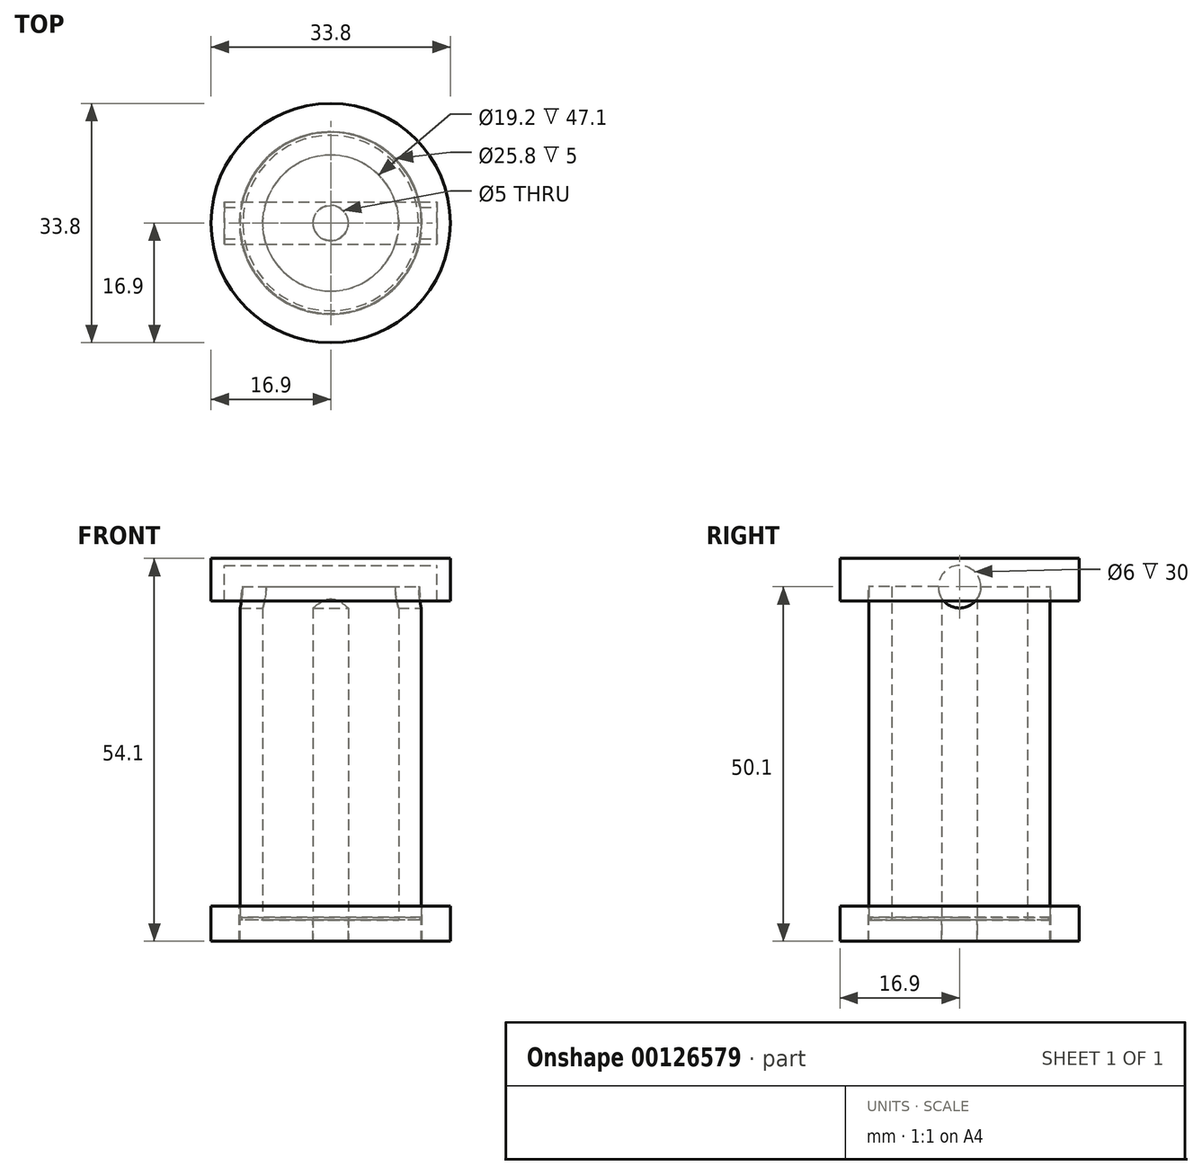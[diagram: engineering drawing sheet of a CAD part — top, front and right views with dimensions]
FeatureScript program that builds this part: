
annotation { "Feature Type Name" : "Feature", "Feature Type Description" : "" }
export const myFeature = defineFeature(function(context is Context, id is Id, definition is map)
    precondition{}
    {
        {
            var Q0;
            Q0=qCreatedBy(makeId("Top.planeOp"),FACE);
            var sketch = newSketch(context, id + "F0", { "sketchPlane" : qUnion([Q0])});
            skCircle(sketch, "E0", {"center": v(0, 0) * mm, "radius": 9.6 * mm});
            skCircle(sketch, "E1", {"center": v(0, 0) * mm, "radius": 12.8 * mm});
            skCircle(sketch, "E2", {"center": v(0, 0) * mm, "radius": 2.5 * mm});
            skSolve(sketch);
        }
        {
            var Q0;
            Q0=makeQuery(id+"F0.imprint","IMPRINT",FACE,{"disambiguationData":[TD([[makeQuery(id+"F0.imprint","IMPRINT",EDGE,{"derivedFrom":sQuery(id+"F0.wireOp",EDGE,"E0")}),-1.0]])]});
            var Q1;
            Q1=makeQuery(id+"F0.imprint","IMPRINT",FACE,{"disambiguationData":[TD([[makeQuery(id+"F0.imprint","IMPRINT",EDGE,{"derivedFrom":sQuery(id+"F0.wireOp",EDGE,"E2")}),1.0]])]});
            extrude(context, id + "F1", {"entities" : qUnion([Q0, Q1]), "depth" : 47.1 * mm, "symmetric" : true});
        }
        {
            var Q0;
            Q0=makeQuery(id+"F1.opExtrude","CAP_FACE",FACE,{"disambiguationData":[OSD([sQuery(id+"F0.wireOp",EDGE,"E2")])],"isStart":false});
            var sketch = newSketch(context, id + "F2", { "sketchPlane" : qUnion([Q0])});
            skCircle(sketch, "E3", {"center": v(0, 0) * mm, "radius": 16.9 * mm});
            skCircle(sketch, "E4", {"center": v(0, 0) * mm, "radius": 12.9 * mm});
            skSolve(sketch);
        }
        {
            var Q0;
            Q0=makeQuery(id+"F2.imprint","IMPRINT",FACE,{"disambiguationData":[TD([[makeQuery(id+"F2.imprint","IMPRINT",EDGE,{"derivedFrom":sQuery(id+"F2.wireOp",EDGE,"E4")}),1.0]])]});
            var Q1;
            Q1=makeQuery(id+"F2.imprint","IMPRINT",FACE,{"disambiguationData":[TD([[makeQuery(id+"F2.imprint","IMPRINT",EDGE,{"derivedFrom":makeQuery(id+"F1.opExtrude","CAP_EDGE",EDGE,{"disambiguationData":[OSD([sQuery(id+"F0.wireOp",EDGE,"E2")])],"isStart":false})}),1.0]])]});
            var Q2;
            Q2=makeQuery(id+"F2.imprint","IMPRINT",FACE,{"disambiguationData":[TD([[makeQuery(id+"F2.imprint","IMPRINT",EDGE,{"derivedFrom":sQuery(id+"F2.wireOp",EDGE,"E3")}),1.0]])]});
            extrude(context, id + "F3", {"entities" : qUnion([Q0, Q1, Q2]), "operationType" : NewBodyOperationType.ADD, "depth" : 4 * mm});
        }
        {
            var Q0;
            Q0=makeQuery(id+"F2.imprint","IMPRINT",FACE,{"disambiguationData":[TD([[makeQuery(id+"F2.imprint","IMPRINT",EDGE,{"derivedFrom":sQuery(id+"F2.wireOp",EDGE,"E3")}),1.0]])]});
            extrude(context, id + "F4", {"entities" : qUnion([Q0]), "operationType" : NewBodyOperationType.ADD, "oppositeDirection" : true, "depth" : 2 * mm});
        }
        {
            var Q0;
            Q0=makeQuery(id+"F1.opExtrude","CAP_FACE",FACE,{"disambiguationData":[OSD([sQuery(id+"F0.wireOp",EDGE,"E2")])],"isStart":true});
            extrude(context, id + "F5", {"entities" : qUnion([Q0]), "operationType" : NewBodyOperationType.ADD, "depth" : 3 * mm});
        }
        {
            var Q0;
            Q0=makeQuery(id+"F1.opExtrude","CAP_FACE",FACE,{"disambiguationData":[OSD([sQuery(id+"F0.wireOp",EDGE,"E0"),sQuery(id+"F0.wireOp",EDGE,"E1")])],"isStart":true});
            var sketch = newSketch(context, id + "F6", { "sketchPlane" : qUnion([Q0])});
            skCircle(sketch, "E5.0", {"center": v(0, 0) * mm, "radius": 9.6 * mm});
            skCircle(sketch, "E5.1", {"center": v(0, 0) * mm, "radius": 16.9 * mm});
            skCircle(sketch, "E6.0", {"center": v(0, 0) * mm, "radius": 2.5 * mm});
            skCircle(sketch, "E7.0", {"center": v(0, 0) * mm, "radius": 12.9 * mm});
            skSolve(sketch);
        }
        {
            var Q0;
            Q0=makeQuery(id+"F6.imprint","IMPRINT",FACE,{"disambiguationData":[TD([[makeQuery(id+"F6.imprint","IMPRINT",EDGE,{"derivedFrom":sQuery(id+"F6.wireOp",EDGE,"E5.1")}),1.0]])]});
            var Q1;
            Q1=makeQuery(id+"F6.imprint","IMPRINT",FACE,{"disambiguationData":[TD([[makeQuery(id+"F6.imprint","IMPRINT",EDGE,{"derivedFrom":sQuery(id+"F6.wireOp",EDGE,"E5.0")}),1.0]])]});
            var Q2;
            Q2=makeQuery(id+"F6.imprint","IMPRINT",FACE,{"disambiguationData":[TD([[makeQuery(id+"F6.imprint","IMPRINT",EDGE,{"derivedFrom":sQuery(id+"F6.wireOp",EDGE,"E5.0")}),-1.0]])]});
            var Q3;
            Q3=makeQuery(id+"F6.imprint","IMPRINT",FACE,{"disambiguationData":[TD([[makeQuery(id+"F6.imprint","IMPRINT",EDGE,{"derivedFrom":sQuery(id+"F6.wireOp",EDGE,"E7.0")}),-1.0]])]});
            extrude(context, id + "F7", {"entities" : qUnion([Q0, Q1, Q2, Q3]), "depth" : 3 * mm});
        }
        {
            var Q0;
            Q0=makeQuery(id+"F6.imprint","IMPRINT",FACE,{"disambiguationData":[TD([[makeQuery(id+"F6.imprint","IMPRINT",EDGE,{"derivedFrom":sQuery(id+"F6.wireOp",EDGE,"E5.1")}),1.0]])]});
            extrude(context, id + "F8", {"entities" : qUnion([Q0]), "operationType" : NewBodyOperationType.ADD, "oppositeDirection" : true, "depth" : 2 * mm});
        }
        {
            var Q0;
            Q0=makeQuery(id+"F1.opExtrude","CAP_EDGE",EDGE,{"disambiguationData":[OSD([sQuery(id+"F0.wireOp",EDGE,"E1")])],"isStart":false});
            var Q1;
            Q1=makeQuery(id+"F1.opExtrude","CAP_EDGE",EDGE,{"disambiguationData":[OSD([sQuery(id+"F0.wireOp",EDGE,"E1")])],"isStart":true});
            chamfer(context, id + "F9", {"entities" : qUnion([Q0, Q1]), "width" : 0.4 * mm, "tangentPropagation" : true});
        }
        {
            var Q0;
            Q0=qCreatedBy(makeId("Right.planeOp"),FACE);
            var sketch = newSketch(context, id + "F10", { "sketchPlane" : qUnion([Q0])});
            skCircle(sketch, "E8", {"center": v(0, 23.55) * mm, "radius": 3 * mm});
            skSolve(sketch);
        }
        {
            var Q0;
            Q0=makeQuery(id+"F10.imprint","IMPRINT",FACE,{"disambiguationData":[TD([[makeQuery(id+"F10.imprint","IMPRINT",EDGE,{"derivedFrom":sQuery(id+"F10.wireOp",EDGE,"E8")}),1.0]])]});
            extrude(context, id + "F11", {"entities" : qUnion([Q0]), "operationType" : NewBodyOperationType.REMOVE, "oppositeDirection" : true, "depth" : 30 * mm, "symmetric" : true});
        }
    });
